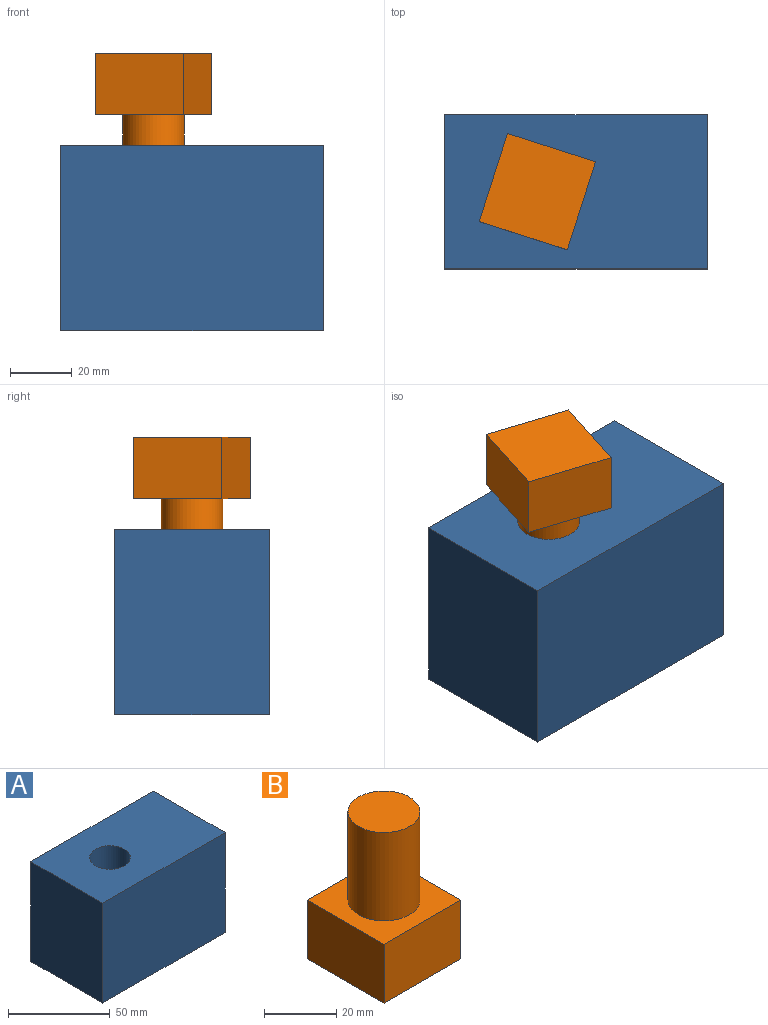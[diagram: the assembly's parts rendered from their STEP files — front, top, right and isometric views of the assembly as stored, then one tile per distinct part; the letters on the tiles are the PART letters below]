
ASSEMBLY  parts=2 mates=1
PART A: 8 faces, bbox 85x50x60 mm
  f0: plane 85x60mm, normal (0,-1,0), area 5100mm2, adj f2,f3,f4,f7
  f1: plane 85x60mm, normal (0,1,0), area 5100mm2, adj f2,f3,f4,f7
  f2: plane 60x50mm, normal (-1,0,0), area 3000mm2, adj f0,f1,f3,f4
  f3: plane 85x50mm, normal (0,0,1), area 3935.8mm2, adj f0,f1,f2,f5,f7
  f4: plane 85x50mm, normal (0,0,-1), area 4250mm2, adj f0,f1,f2,f7
  f5: cylinder r=10mm len=25mm, axis (0,0,1), area 1570.8mm2, adj f3,f6
  f6: plane 20x20mm, normal (0,0,1), area 314.2mm2, adj f5
  f7: plane 60x50mm, normal (1,0,0), area 3000mm2, adj f0,f1,f3,f4
PART B: 8 faces, bbox 30x30x50 mm
  f0: plane 30x20mm, normal (0,-1,0), area 600mm2, adj f1,f3,f4,f5
  f1: plane 30x20mm, normal (1,0,0), area 600mm2, adj f0,f2,f4,f5
  f2: plane 30x20mm, normal (0,1,0), area 600mm2, adj f1,f3,f4,f5
  f3: plane 30x20mm, normal (-1,0,0), area 600mm2, adj f0,f2,f4,f5
  f4: plane 30x30mm, normal (0,0,1), area 585.8mm2, adj f0,f1,f2,f3,f6
  f5: plane 30x30mm, normal (0,0,-1), area 900mm2, adj f0,f1,f2,f3
  f6: cylinder r=10mm len=30mm, axis (0,0,-1), area 1885mm2, adj f4,f7
  f7: plane 20x20mm, normal (0,0,1), area 314.2mm2, adj f6
PLACE A t=(-30.97,0.55,-13.17)mm fixed
PLACE B rot(axis=(-0.81,-0.59,0),180deg) t=(-30.97,0.55,76.81)mm
MATE cylindrical A.f5 <-> B.f6  axis (0,0,1) through (-30.97,0.55,46.83)mm
